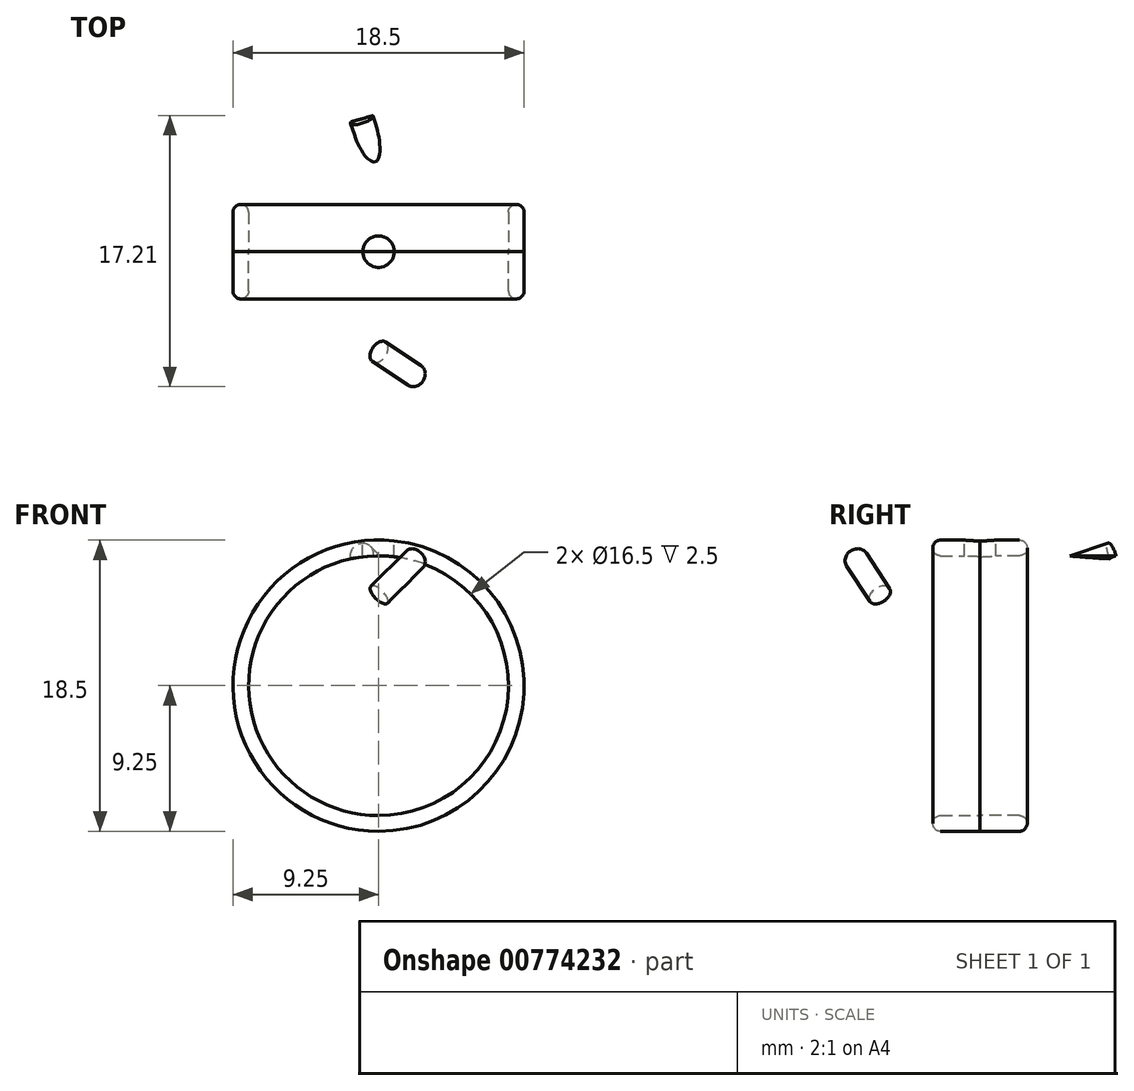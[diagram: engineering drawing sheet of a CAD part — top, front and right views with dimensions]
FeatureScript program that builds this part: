
annotation { "Feature Type Name" : "Feature", "Feature Type Description" : "" }
export const myFeature = defineFeature(function(context is Context, id is Id, definition is map)
    precondition{}
    {
        {
            var Q0;
            Q0=qCreatedBy(makeId("Front.planeOp"),FACE);
            var sketch = newSketch(context, id + "F0", { "sketchPlane" : qUnion([Q0])});
            skCircle(sketch, "E0", {"center": v(0, 0) * mm, "radius": 8.25 * mm});
            skCircle(sketch, "E1", {"center": v(0, 0) * mm, "radius": 9.25 * mm});
            skSolve(sketch);
        }
        {
            var Q0;
            Q0=qSketchRegion(id+"F0",true);
            extrude(context, id + "F1", {"entities" : qUnion([Q0]), "depth" : 3 * mm, "offsetDistance" : 25 * mm});
        }
        {
            var Q0;
            Q0=makeQuery(id+"F1.opExtrude","CAP_FACE",FACE,{"disambiguationData":[OSD([sQuery(id+"F0.wireOp",EDGE,"E0"),sQuery(id+"F0.wireOp",EDGE,"E1")])],"isStart":false});
            cPlane(context, id + "F2", {"entities" : qUnion([Q0]), "cplaneType" : CPlaneType.OFFSET, "offset" : 2.25 * mm, "oppositeDirection" : true, "width" : 150 * mm, "height" : 150 * mm});
        }
        {
            var Q0;
            Q0=qCreatedBy(id+"F2.planeOp",FACE);
            var sketch = newSketch(context, id + "F3", { "sketchPlane" : qUnion([Q0])});
            skLineSegment(sketch, "E2", {"start": v(0, 15) * mm, "end": v(0, -15.53) * mm, "construction": true});
            skLineSegment(sketch, "E3", {"start": v(0.3, 7.78) * mm, "end": v(1, 8.5) * mm});
            skLineSegment(sketch, "E4", {"start": v(-0.3, 7.78) * mm, "end": v(-1, 8.5) * mm});
            skSolve(sketch);
        }
        {
            var Q0;
            Q0=sQuery(id+"F3.wireOp",EDGE,"E3");
            cPlane(context, id + "F4", {"entities" : qUnion([Q0]), "cplaneType" : CPlaneType.LINE_ANGLE, "offset" : 25 * mm, "angle" : 90 * degree, "oppositeDirection" : true, "width" : 150 * mm, "height" : 150 * mm});
        }
        {
            var Q0;
            Q0=sQuery(id+"F3.wireOp",EDGE,"E4");
            cPlane(context, id + "F5", {"entities" : qUnion([Q0]), "cplaneType" : CPlaneType.LINE_ANGLE, "offset" : 25 * mm, "angle" : 90 * degree, "oppositeDirection" : true, "width" : 150 * mm, "height" : 150 * mm});
        }
        {
            var Q0;
            Q0=qCreatedBy(id+"F4.planeOp",FACE);
            var sketch = newSketch(context, id + "F6", { "sketchPlane" : qUnion([Q0])});
            skLineSegment(sketch, "E5", {"start": v(-0.75, 6.71) * mm, "end": v(-0.75, 6.72) * mm});
            skLineSegment(sketch, "E6", {"start": v(-0.75, 6.72) * mm, "end": v(-2.44, 10.35) * mm});
            skSolve(sketch);
        }
        {
            var Q0;
            Q0=qCreatedBy(id+"F5.planeOp",FACE);
            var sketch = newSketch(context, id + "F7", { "sketchPlane" : qUnion([Q0])});
            skLineSegment(sketch, "E7", {"start": v(-6.71, 0.75) * mm, "end": v(-6.71, 0.76) * mm});
            skLineSegment(sketch, "E8", {"start": v(-6.71, 0.76) * mm, "end": v(-10.34, 2.45) * mm});
            skSolve(sketch);
        }
        {
            var Q0;
            Q0=sQuery(id+"F6.wireOp",VERTEX,"E6.end");
            var Q1;
            Q1=sQuery(id+"F6.wireOp",EDGE,"E6");
            cPlane(context, id + "F8", {"entities" : qUnion([Q0, Q1]), "cplaneType" : CPlaneType.LINE_POINT, "offset" : 25 * mm, "width" : 150 * mm, "height" : 150 * mm});
        }
        {
            var Q0;
            Q0=sQuery(id+"F7.wireOp",VERTEX,"E8.end");
            var Q1;
            Q1=sQuery(id+"F7.wireOp",EDGE,"E8");
            cPlane(context, id + "F9", {"entities" : qUnion([Q0, Q1]), "cplaneType" : CPlaneType.LINE_POINT, "offset" : 25 * mm, "width" : 150 * mm, "height" : 150 * mm});
        }
        {
            var Q0;
            Q0=qCreatedBy(id+"F8.planeOp",FACE);
            var sketch = newSketch(context, id + "F10", { "sketchPlane" : qUnion([Q0])});
            skCircle(sketch, "E9", {"center": v(-4.04, 4.05) * mm, "radius": 0.75 * mm});
            skSolve(sketch);
        }
        {
            var Q0;
            Q0=qCreatedBy(id+"F9.planeOp",FACE);
            var sketch = newSketch(context, id + "F11", { "sketchPlane" : qUnion([Q0])});
            skCircle(sketch, "E10", {"center": v(-2.15, 5.3) * mm, "radius": 0.75 * mm});
            skSolve(sketch);
        }
        {
            var Q0;
            Q0=makeQuery(id+"F10.imprint","IMPRINT",FACE,{"disambiguationData":[TD([[makeQuery(id+"F10.imprint","IMPRINT",EDGE,{"derivedFrom":sQuery(id+"F10.wireOp",EDGE,"E9")}),1.0]])]});
            var Q1;
            Q1=sQuery(id+"F6.wireOp",EDGE,"E6");
            sweep(context, id + "F12", {"operationType" : NewBodyOperationType.ADD, "profiles" : qUnion([Q0]), "path" : qUnion([Q1])});
        }
        {
            var Q0;
            Q0=makeQuery(id+"F11.imprint","IMPRINT",FACE,{"disambiguationData":[TD([[makeQuery(id+"F11.imprint","IMPRINT",EDGE,{"derivedFrom":sQuery(id+"F11.wireOp",EDGE,"E10")}),1.0]])]});
            var Q1;
            Q1=sQuery(id+"F7.wireOp",EDGE,"E8");
            sweep(context, id + "F13", {"operationType" : NewBodyOperationType.ADD, "profiles" : qUnion([Q0]), "path" : qUnion([Q1])});
        }
        {
            var Q0;
            Q0=qCreatedBy(makeId("Top.planeOp"),FACE);
            cPlane(context, id + "F14", {"entities" : qUnion([Q0]), "cplaneType" : CPlaneType.OFFSET, "offset" : 13 * mm, "width" : 150 * mm, "height" : 150 * mm});
        }
        {
            var Q0;
            Q0=qCreatedBy(id+"F14.planeOp",FACE);
            var sketch = newSketch(context, id + "F15", { "sketchPlane" : qUnion([Q0])});
            skCircle(sketch, "E11", {"center": v(0, 0) * mm, "radius": 1 * mm});
            skSolve(sketch);
        }
        {
            var Q0;
            Q0=qSketchRegion(id+"F15",true);
            extrude(context, id + "F16", {"entities" : qUnion([Q0]), "operationType" : NewBodyOperationType.REMOVE, "oppositeDirection" : true, "depth" : 9 * mm, "offsetDistance" : 25 * mm});
        }
        {
            var Q0;
            Q0=makeQuery(id+"F1.opExtrude","SWEPT_BODY",BODY,{"disambiguationData":[OSD([sQuery(id+"F0.wireOp",EDGE,"E0"),sQuery(id+"F0.wireOp",EDGE,"E1")])]});
            var Q1;
            Q1=makeQuery(id+"F1.opExtrude","CAP_FACE",FACE,{"disambiguationData":[OSD([sQuery(id+"F0.wireOp",EDGE,"E0"),sQuery(id+"F0.wireOp",EDGE,"E1")])],"isStart":true});
            mirror(context, id + "F17", {"operationType" : NewBodyOperationType.ADD, "entities" : qUnion([Q0]), "mirrorPlane" : qUnion([Q1])});
        }
        {
            var Q0;
            Q0=makeQuery(id+"F1.opExtrude","CAP_FACE",FACE,{"disambiguationData":[OSD([sQuery(id+"F0.wireOp",EDGE,"E0"),sQuery(id+"F0.wireOp",EDGE,"E1")])],"isStart":false});
            var sketch = newSketch(context, id + "F18", { "sketchPlane" : qUnion([Q0])});
            skCircle(sketch, "E12", {"center": v(0, 0) * mm, "radius": 8.25 * mm});
            skSolve(sketch);
        }
        {
            var Q0;
            Q0=qSketchRegion(id+"F18",true);
            extrude(context, id + "F19", {"entities" : qUnion([Q0]), "operationType" : NewBodyOperationType.REMOVE, "oppositeDirection" : true, "depth" : 25 * mm, "offsetDistance" : 25 * mm});
        }
        {
            var Q0;
            Q0=makeQuery(id+"F1.opExtrude","CAP_FACE",FACE,{"disambiguationData":[OSD([sQuery(id+"F0.wireOp",EDGE,"E0"),sQuery(id+"F0.wireOp",EDGE,"E1")])],"isStart":false});
            var Q1;
            Q1=makeQuery(id+"F17.opPattern","COPY",FACE,{"derivedFrom":makeQuery(id+"F1.opExtrude","CAP_FACE",FACE,{"disambiguationData":[OSD([sQuery(id+"F0.wireOp",EDGE,"E0"),sQuery(id+"F0.wireOp",EDGE,"E1")])],"isStart":false}),"instanceName":"1"});
            var Q2;
            Q2=makeQuery(id+"F17.opPattern","COPY",FACE,{"derivedFrom":makeQuery(id+"F12.opSweep","CAP_FACE",FACE,{"disambiguationData":[OSD([sQuery(id+"F6.wireOp",VERTEX,"E6.end"),sQuery(id+"F10.wireOp",EDGE,"E9")])],"isStart":true}),"instanceName":"1"});
            var Q3;
            Q3=makeQuery(id+"F12.opSweep","CAP_FACE",FACE,{"disambiguationData":[OSD([sQuery(id+"F6.wireOp",VERTEX,"E6.end"),sQuery(id+"F10.wireOp",EDGE,"E9")])],"isStart":true});
            var Q4;
            Q4=makeQuery(id+"F13.opSweep","CAP_FACE",FACE,{"disambiguationData":[OSD([sQuery(id+"F7.wireOp",VERTEX,"E8.end"),sQuery(id+"F11.wireOp",EDGE,"E10")])],"isStart":true});
            var Q5;
            Q5=makeQuery(id+"F17.opPattern","COPY",FACE,{"derivedFrom":makeQuery(id+"F13.opSweep","CAP_FACE",FACE,{"disambiguationData":[OSD([sQuery(id+"F7.wireOp",VERTEX,"E8.end"),sQuery(id+"F11.wireOp",EDGE,"E10")])],"isStart":true}),"instanceName":"1"});
            fillet(context, id + "F20", {"entities" : qUnion([Q0, Q1, Q2, Q3, Q4, Q5]), "tangentPropagation" : true, "radius" : .5 * mm, "defaultsChanged" : false, "vertexSettings" : [], "allowEdgeOverflow" : false});
        }
    });
